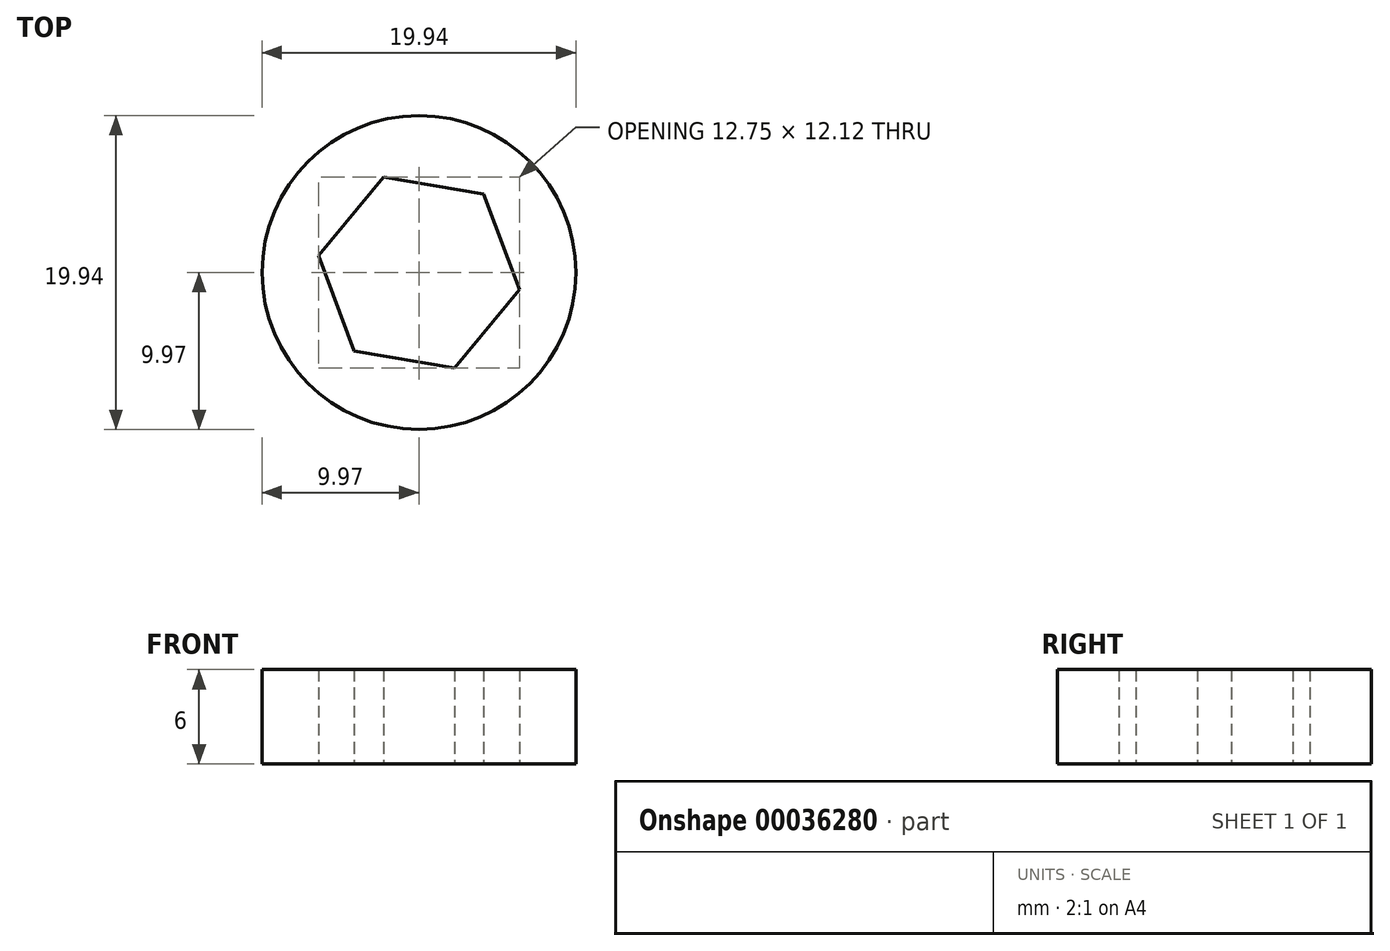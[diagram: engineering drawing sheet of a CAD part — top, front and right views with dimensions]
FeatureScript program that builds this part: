
annotation { "Feature Type Name" : "Feature", "Feature Type Description" : "" }
export const myFeature = defineFeature(function(context is Context, id is Id, definition is map)
    precondition{}
    {
        {
            var Q0;
            Q0=qCreatedBy(makeId("Top.planeOp"),FACE);
            var sketch = newSketch(context, id + "F0", { "sketchPlane" : qUnion([Q0])});
            skCircle(sketch, "E0", {"center": v(0, 0) * mm, "radius": 9.97 * mm});
            skCircle(sketch, "E1.cCircle", {"center": v(0, 0) * mm, "radius": 5.6 * mm, "construction": true});
            skLineSegment(sketch, "E1.0", {"start": v(6.38, -1.07) * mm, "end": v(2.26, -6.06) * mm});
            skLineSegment(sketch, "E1.1", {"start": v(2.26, -6.06) * mm, "end": v(-4.11, -4.99) * mm});
            skLineSegment(sketch, "E1.2", {"start": v(-4.11, -4.99) * mm, "end": v(-6.38, 1.07) * mm});
            skLineSegment(sketch, "E1.3", {"start": v(-6.38, 1.07) * mm, "end": v(-2.26, 6.06) * mm});
            skLineSegment(sketch, "E1.4", {"start": v(-2.26, 6.06) * mm, "end": v(4.11, 4.99) * mm});
            skLineSegment(sketch, "E1.5", {"start": v(4.11, 4.99) * mm, "end": v(6.38, -1.07) * mm});
            skPoint(sketch, "E1.0.midPoint", {"position": v(4.32, -3.56) * mm});
            skSolve(sketch);
        }
        {
            var Q0;
            Q0=makeQuery(id+"F0.imprint","IMPRINT",FACE,{"disambiguationData":[TD([[makeQuery(id+"F0.imprint","IMPRINT",EDGE,{"derivedFrom":sQuery(id+"F0.wireOp",EDGE,"E0")}),1.0]])]});
            extrude(context, id + "F1", {"entities" : qUnion([Q0]), "depth" : 6 * mm});
        }
    });
